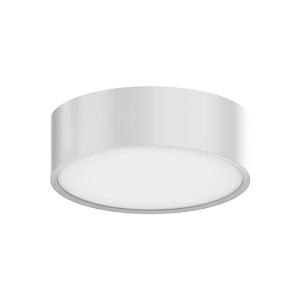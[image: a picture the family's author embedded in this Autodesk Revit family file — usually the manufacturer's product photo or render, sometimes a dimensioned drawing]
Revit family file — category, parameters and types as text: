
# Revit family: ledceilinglu-e_rd142-18w-840-wh_540001296500
name_source: partatom
category: Leuchten
revit_build: Autodesk Revit 2016 (Build: 20190508_0715(x64)
units: mm (PartAtom-declared; Revit-internal decimal feet)

## family parameters
Basisbauteil = Fläche
Beim Laden mit Abzugskörper schneiden = Nein
Bemaßung runder Anschluss = Durchmesser verwenden
Gemeinsam genutzt = Nein
Lichtquelle = Nein
Raumberechnungspunkt = Nein
Teiletyp = Normal

## types (1)
- LEDCeilingLu-E Rd142-18W-840-WH (1 x LED, 1710 lm)
    Approval mark = CE
    Beschreibung = Stylish and compact ceiling luminaire. Clean “twist-and-lock” mounting system. High quality full metal body. Low height of only 46mm. Suitable for ceiling and wall mounting.
    CIE Flux Codes = 49 80 96 100 100
    Control Gear = Electronic ballast
    Height = 100 mm  [stored 0.328084 ft]
    Hersteller = OPPLE
    Lamp Light Flux = 1710 lm
    Lamp count = 1
    Lampe = 1 x LED
    Length = 100 mm  [stored 0.328084 ft]
    Luminous efficacy = 95 lm/W
    ModVariant = Nein
    Modell = 540001296500
    Mounting Place = Wall, Ceiling
    Mounting Type = Surface mounted
    Number of Poles = 1
    OnlyDefault = Ja
    Power Factor = 1
    Product Name = LEDCeilingLu-E Rd142-18W-840-WH
    Product group = Ceiling Light Luna
    ProductGroupID = 305
    Protection Class = Protection class II
    Protection Degree = IP 20
    RLX_Detail_Level = 1
    RlxData = <blob elided: 125549 chars, md5=291cc432>
    Scheinlast = 18 VA
    Socket = socket
    Standby Power = 0 W
    System Light Flux = 1710 lm
    System Power = 18 W
    Typenbild = luna_wh_rd142.jpg
    Typenkommentare = Product without accessories
    URL = http://relux.com
    VarID = ---
    Voltage = 230 V
    Voltage Range = 220-240 V
    Vorgabe-Ansicht = 1800 mm
    Weight = 0.00 kg
    Width = 100 mm  [stored 0.328084 ft]

note: [stored X ft] marks values corroborated as IEEE doubles in the binary element streams (Revit-internal decimal feet)

## geometry (parser evidence)
native form markers: Blend x4, Sweep x12
no freeform markers — native parametric forms only
